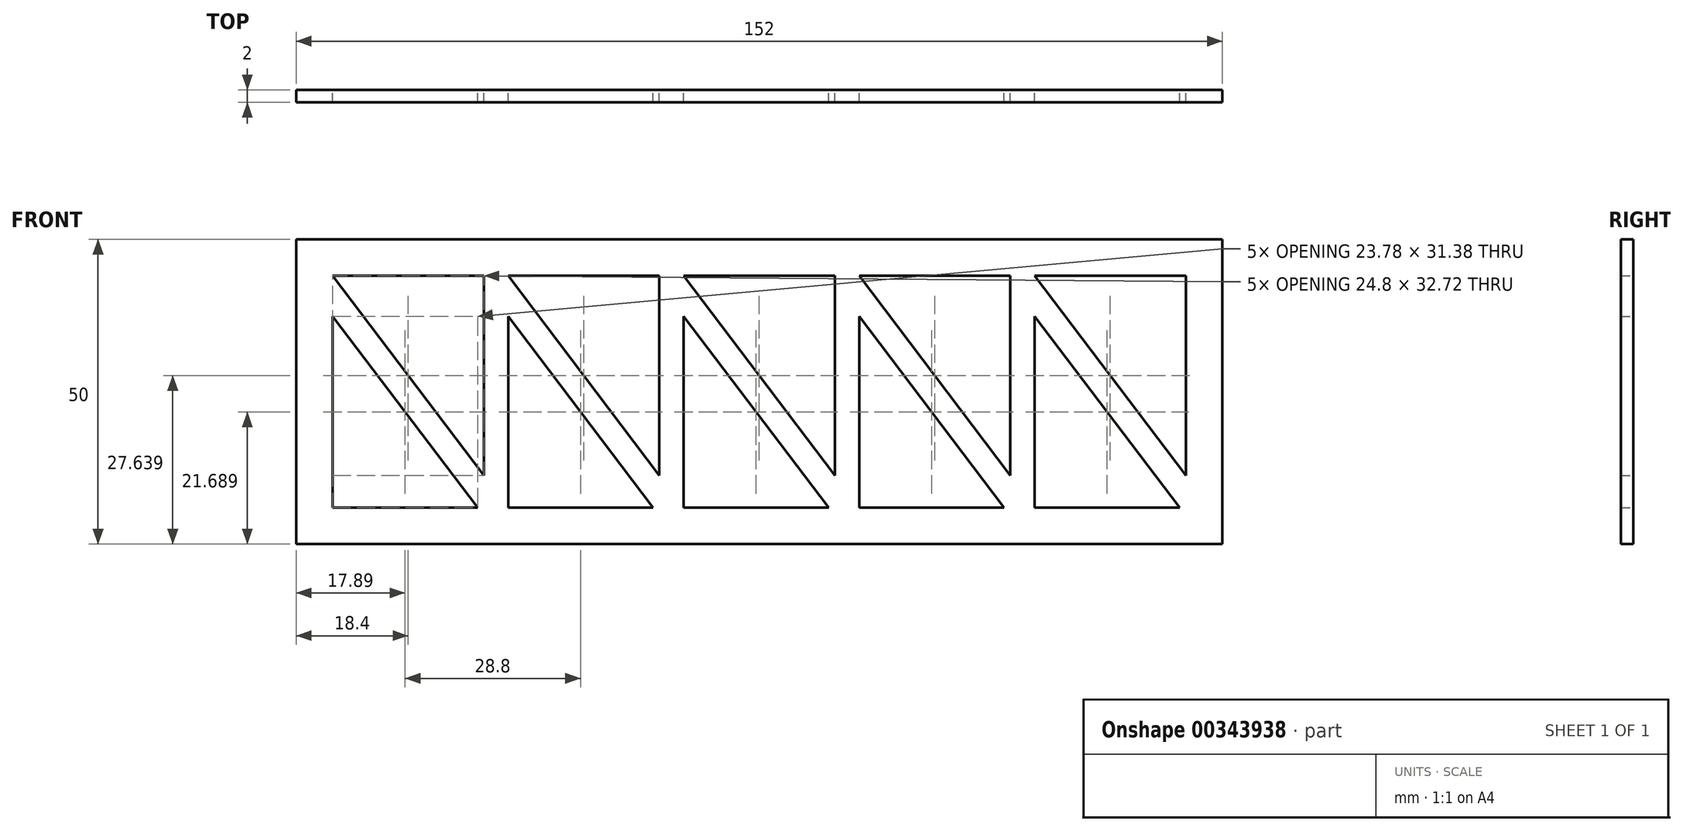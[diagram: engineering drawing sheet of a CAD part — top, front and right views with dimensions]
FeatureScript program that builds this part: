
annotation { "Feature Type Name" : "Feature", "Feature Type Description" : "" }
export const myFeature = defineFeature(function(context is Context, id is Id, definition is map)
    precondition{}
    {
        {
            var Q0;
            Q0=qCreatedBy(makeId("Front.planeOp"),FACE);
            var sketch = newSketch(context, id + "F0", { "sketchPlane" : qUnion([Q0])});
            skLineSegment(sketch, "E0.bottom", {"start": v(0, 0) * mm, "end": v(152, 0) * mm});
            skLineSegment(sketch, "E0.top", {"start": v(0, 50) * mm, "end": v(152, 50) * mm});
            skLineSegment(sketch, "E0.left", {"start": v(0, 0) * mm, "end": v(0, 50) * mm});
            skLineSegment(sketch, "E0.right", {"start": v(152, 0) * mm, "end": v(152, 50) * mm});
            skLineSegment(sketch, "E1.bottom", {"start": v(6, 6) * mm, "end": v(150, 6) * mm});
            skLineSegment(sketch, "E1.top", {"start": v(6, 44) * mm, "end": v(150, 44) * mm});
            skLineSegment(sketch, "E1.left", {"start": v(6, 6) * mm, "end": v(6, 44) * mm});
            skLineSegment(sketch, "E1.right", {"start": v(150, 6) * mm, "end": v(150, 44) * mm});
            skLineSegment(sketch, "E2", {"start": v(6, 44) * mm, "end": v(34.8, 6) * mm});
            skLineSegment(sketch, "E3", {"start": v(34.8, 6) * mm, "end": v(34.8, 44) * mm});
            skLineSegment(sketch, "E4", {"start": v(34.8, 44) * mm, "end": v(63.6, 6) * mm});
            skLineSegment(sketch, "E5", {"start": v(63.6, 6) * mm, "end": v(63.6, 44) * mm});
            skLineSegment(sketch, "E6", {"start": v(63.6, 44) * mm, "end": v(92.4, 6) * mm});
            skLineSegment(sketch, "E7", {"start": v(92.4, 6) * mm, "end": v(92.4, 44) * mm});
            skLineSegment(sketch, "E8", {"start": v(92.4, 44) * mm, "end": v(121.2, 6) * mm});
            skLineSegment(sketch, "E9", {"start": v(121.2, 6) * mm, "end": v(121.2, 44) * mm});
            skLineSegment(sketch, "E10", {"start": v(150, 6) * mm, "end": v(121.2, 44) * mm});
            skLineSegment(sketch, "E11", {"start": v(6, 37.38) * mm, "end": v(29.78, 6) * mm});
            skLineSegment(sketch, "E12", {"start": v(30.8, 11.28) * mm, "end": v(30.8, 44) * mm});
            skLineSegment(sketch, "E13", {"start": v(34.8, 37.38) * mm, "end": v(58.58, 6) * mm});
            skLineSegment(sketch, "E14", {"start": v(59.6, 44) * mm, "end": v(59.6, 11.28) * mm});
            skLineSegment(sketch, "E15", {"start": v(63.6, 37.38) * mm, "end": v(87.38, 6) * mm});
            skLineSegment(sketch, "E16", {"start": v(88.4, 44) * mm, "end": v(88.4, 11.28) * mm});
            skLineSegment(sketch, "E17", {"start": v(92.4, 37.38) * mm, "end": v(116.18, 6) * mm});
            skLineSegment(sketch, "E18", {"start": v(117.2, 44) * mm, "end": v(117.2, 11.28) * mm});
            skLineSegment(sketch, "E19", {"start": v(121.2, 37.38) * mm, "end": v(144.98, 6) * mm});
            skLineSegment(sketch, "E20", {"start": v(146, 44) * mm, "end": v(146, 11.28) * mm});
            skSolve(sketch);
        }
        {
            var Q0;
            Q0=makeQuery(id+"F0.imprint","IMPRINT",FACE,{"disambiguationData":[TD([[makeQuery(id+"F0.imprint","IMPRINT",EDGE,{"derivedFrom":sQuery(id+"F0.wireOp",EDGE,"E0.bottom")}),1.0]])]});
            var Q1;
            {var subQ0=sQuery(id+"F0.wireOp",EDGE,"E10");Q1=makeQuery(id+"F0.imprint","IMPRINT",FACE,{"disambiguationData":[TD([[makeQuery(id+"F0.imprint","IMPRINT",EDGE,{"derivedFrom":subQ0}),1.0]])]});}
            var Q2;
            {var subQ4=sQuery(id+"F0.wireOp",EDGE,"E18");Q2=makeQuery(id+"F0.imprint","IMPRINT",FACE,{"disambiguationData":[TD([[makeQuery(id+"F0.imprint","IMPRINT",EDGE,{"derivedFrom":subQ4}),1.0]])]});}
            var Q3;
            {var subQ6=sQuery(id+"F0.wireOp",EDGE,"E17");Q3=makeQuery(id+"F0.imprint","IMPRINT",FACE,{"disambiguationData":[TD([[makeQuery(id+"F0.imprint","IMPRINT",EDGE,{"derivedFrom":subQ6}),1.0]])]});}
            var Q4;
            {var subQ4=sQuery(id+"F0.wireOp",EDGE,"E16");Q4=makeQuery(id+"F0.imprint","IMPRINT",FACE,{"disambiguationData":[TD([[makeQuery(id+"F0.imprint","IMPRINT",EDGE,{"derivedFrom":subQ4}),1.0]])]});}
            var Q5;
            {var subQ6=sQuery(id+"F0.wireOp",EDGE,"E15");Q5=makeQuery(id+"F0.imprint","IMPRINT",FACE,{"disambiguationData":[TD([[makeQuery(id+"F0.imprint","IMPRINT",EDGE,{"derivedFrom":subQ6}),1.0]])]});}
            var Q6;
            {var subQ6=sQuery(id+"F0.wireOp",EDGE,"E14");Q6=makeQuery(id+"F0.imprint","IMPRINT",FACE,{"disambiguationData":[TD([[makeQuery(id+"F0.imprint","IMPRINT",EDGE,{"derivedFrom":subQ6}),1.0]])]});}
            var Q7;
            {var subQ6=sQuery(id+"F0.wireOp",EDGE,"E13");Q7=makeQuery(id+"F0.imprint","IMPRINT",FACE,{"disambiguationData":[TD([[makeQuery(id+"F0.imprint","IMPRINT",EDGE,{"derivedFrom":subQ6}),1.0]])]});}
            var Q8;
            {var subQ6=sQuery(id+"F0.wireOp",EDGE,"E12");Q8=makeQuery(id+"F0.imprint","IMPRINT",FACE,{"disambiguationData":[TD([[makeQuery(id+"F0.imprint","IMPRINT",EDGE,{"derivedFrom":subQ6}),-1.0]])]});}
            var Q9;
            {var subQ4=sQuery(id+"F0.wireOp",EDGE,"E11");Q9=makeQuery(id+"F0.imprint","IMPRINT",FACE,{"disambiguationData":[TD([[makeQuery(id+"F0.imprint","IMPRINT",EDGE,{"derivedFrom":subQ4}),1.0]])]});}
            var Q10;
            {var subQ0=sQuery(id+"F0.wireOp",EDGE,"E1.right");Q10=makeQuery(id+"F0.imprint","IMPRINT",FACE,{"disambiguationData":[TD([[makeQuery(id+"F0.imprint","IMPRINT",EDGE,{"derivedFrom":subQ0}),1.0]])]});}
            extrude(context, id + "F1", {"entities" : qUnion([Q0, Q1, Q2, Q3, Q4, Q5, Q6, Q7, Q8, Q9, Q10]), "depth" : 2 * mm});
        }
    });
